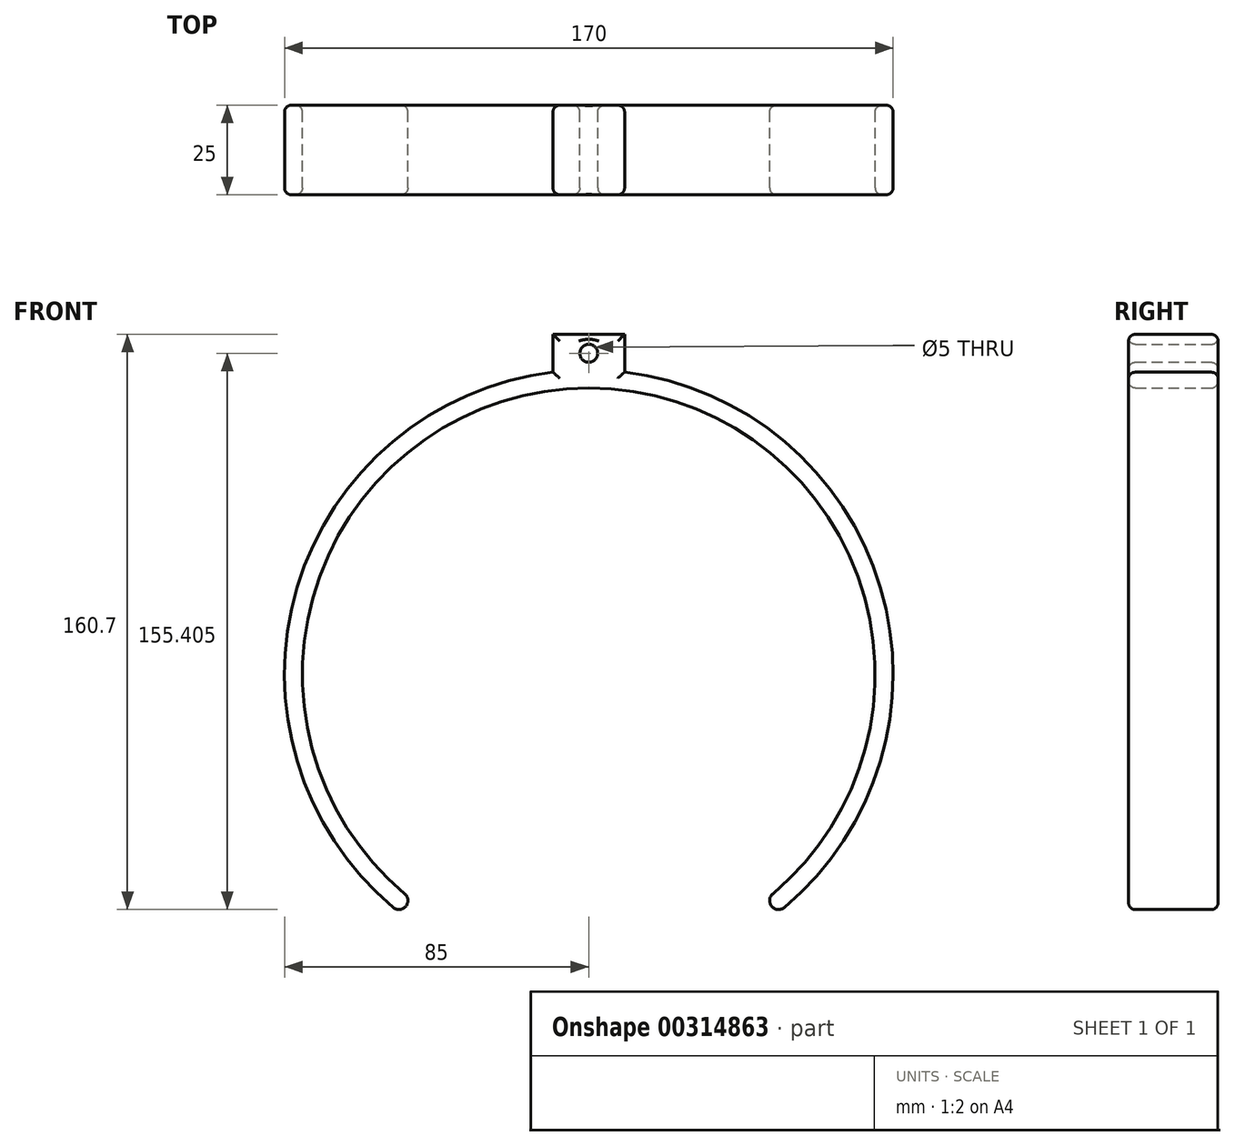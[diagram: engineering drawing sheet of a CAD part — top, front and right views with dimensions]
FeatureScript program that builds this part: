
annotation { "Feature Type Name" : "Feature", "Feature Type Description" : "" }
export const myFeature = defineFeature(function(context is Context, id is Id, definition is map)
    precondition{}
    {
        {
            var Q0;
            Q0=qCreatedBy(makeId("Front.planeOp"),FACE);
            var sketch = newSketch(context, id + "F0", { "sketchPlane" : qUnion([Q0])});
            skArc(sketch, "E0", {"start": v(80, 0) * mm, "mid": v(0, 80) * mm, "end": v(-80, 0) * mm});
            skArc(sketch, "E1", {"start": v(-10, 84.4) * mm, "mid": v(-63.54, 56.46) * mm, "end": v(-85, 0) * mm});
            skLineSegment(sketch, "E2", {"start": v(0, 0) * mm, "end": v(0, 95) * mm, "construction": true});
            skLineSegment(sketch, "E3", {"start": v(0, 95) * mm, "end": v(-10, 95) * mm});
            skLineSegment(sketch, "E4", {"start": v(0, 95) * mm, "end": v(10, 95) * mm});
            skLineSegment(sketch, "E5", {"start": v(-10, 95) * mm, "end": v(-10, 84.4) * mm});
            skLineSegment(sketch, "E6", {"start": v(10, 95) * mm, "end": v(10, 84.4) * mm});
            skLineSegment(sketch, "E7", {"start": v(-10, 95) * mm, "end": v(10, 84.4) * mm, "construction": true});
            skLineSegment(sketch, "E8", {"start": v(10, 95) * mm, "end": v(-10, 84.4) * mm, "construction": true});
            skCircle(sketch, "E9", {"center": v(0, 89.7) * mm, "radius": 2.5 * mm, "construction": true});
            skArc(sketch, "E10.trimOffspring", {"start": v(85, 0) * mm, "mid": v(63.54, 56.46) * mm, "end": v(10, 84.4) * mm});
            skCircle(sketch, "E11", {"center": v(0, 89.7) * mm, "radius": 2.5 * mm});
            skPoint(sketch, "E12.start.orphan", {"position": v(-82.5, 0) * mm});
            skPoint(sketch, "E13.center.orphan", {"position": v(82.5, 0) * mm});
            skArc(sketch, "E14", {"start": v(51.42, -61.28) * mm, "mid": v(0, 80) * mm, "end": v(-51.42, -61.28) * mm});
            skArc(sketch, "E15", {"start": v(-10, 84.4) * mm, "mid": v(-81.45, 24.31) * mm, "end": v(-54.64, -65.11) * mm});
            skLineSegment(sketch, "E16", {"start": v(-51.42, -61.28) * mm, "end": v(-54.64, -65.11) * mm, "construction": true});
            skLineSegment(sketch, "E17", {"start": v(51.42, -61.28) * mm, "end": v(54.64, -65.11) * mm, "construction": true});
            skArc(sketch, "E18.trimOffspring", {"start": v(54.64, -65.11) * mm, "mid": v(81.45, 24.31) * mm, "end": v(10, 84.4) * mm});
            skArc(sketch, "E19", {"start": v(-54.64, -65.11) * mm, "mid": v(-51.11, -64.8) * mm, "end": v(-51.42, -61.28) * mm});
            skArc(sketch, "E20", {"start": v(51.42, -61.28) * mm, "mid": v(51.11, -64.8) * mm, "end": v(54.64, -65.11) * mm});
            skSolve(sketch);
        }
        {
            var Q0;
            Q0 = qSketchRegion(id + "F0", true);
            extrude(context, id + "F1", {"entities" : qUnion([Q0]), "depth" : 25 * mm});
        }
        {
            var Q0;
            Q0=makeQuery(id+"F1.opExtrude","CAP_FACE",FACE,{"disambiguationData":[OSD([sQuery(id+"F0.wireOp",EDGE,"E0"),sQuery(id+"F0.wireOp",EDGE,"E1"),sQuery(id+"F0.wireOp",EDGE,"E3"),sQuery(id+"F0.wireOp",EDGE,"E4"),sQuery(id+"F0.wireOp",EDGE,"E5"),sQuery(id+"F0.wireOp",EDGE,"E6"),sQuery(id+"F0.wireOp",EDGE,"1YMCZduU-x7T9-duUi-XEHQ-A0dn9VgeASlu"),sQuery(id+"F0.wireOp",EDGE,"E13"),sQuery(id+"F0.wireOp",EDGE,"E10.trimOffspring"),sQuery(id+"F0.wireOp",EDGE,"E11")])],"isStart":false});
            var Q1;
            Q1=makeQuery(id+"F1.opExtrude","CAP_FACE",FACE,{"disambiguationData":[OSD([sQuery(id+"F0.wireOp",EDGE,"E0"),sQuery(id+"F0.wireOp",EDGE,"E1"),sQuery(id+"F0.wireOp",EDGE,"E3"),sQuery(id+"F0.wireOp",EDGE,"E4"),sQuery(id+"F0.wireOp",EDGE,"E5"),sQuery(id+"F0.wireOp",EDGE,"E6"),sQuery(id+"F0.wireOp",EDGE,"1YMCZduU-x7T9-duUi-XEHQ-A0dn9VgeASlu"),sQuery(id+"F0.wireOp",EDGE,"E13"),sQuery(id+"F0.wireOp",EDGE,"E10.trimOffspring"),sQuery(id+"F0.wireOp",EDGE,"E11")])],"isStart":true});
            fillet(context, id + "F2", {"entities" : qUnion([Q0, Q1]), "radius" : 1.9 * mm, "tangentPropagation" : true, "allowEdgeOverflow" : false});
        }
    });
